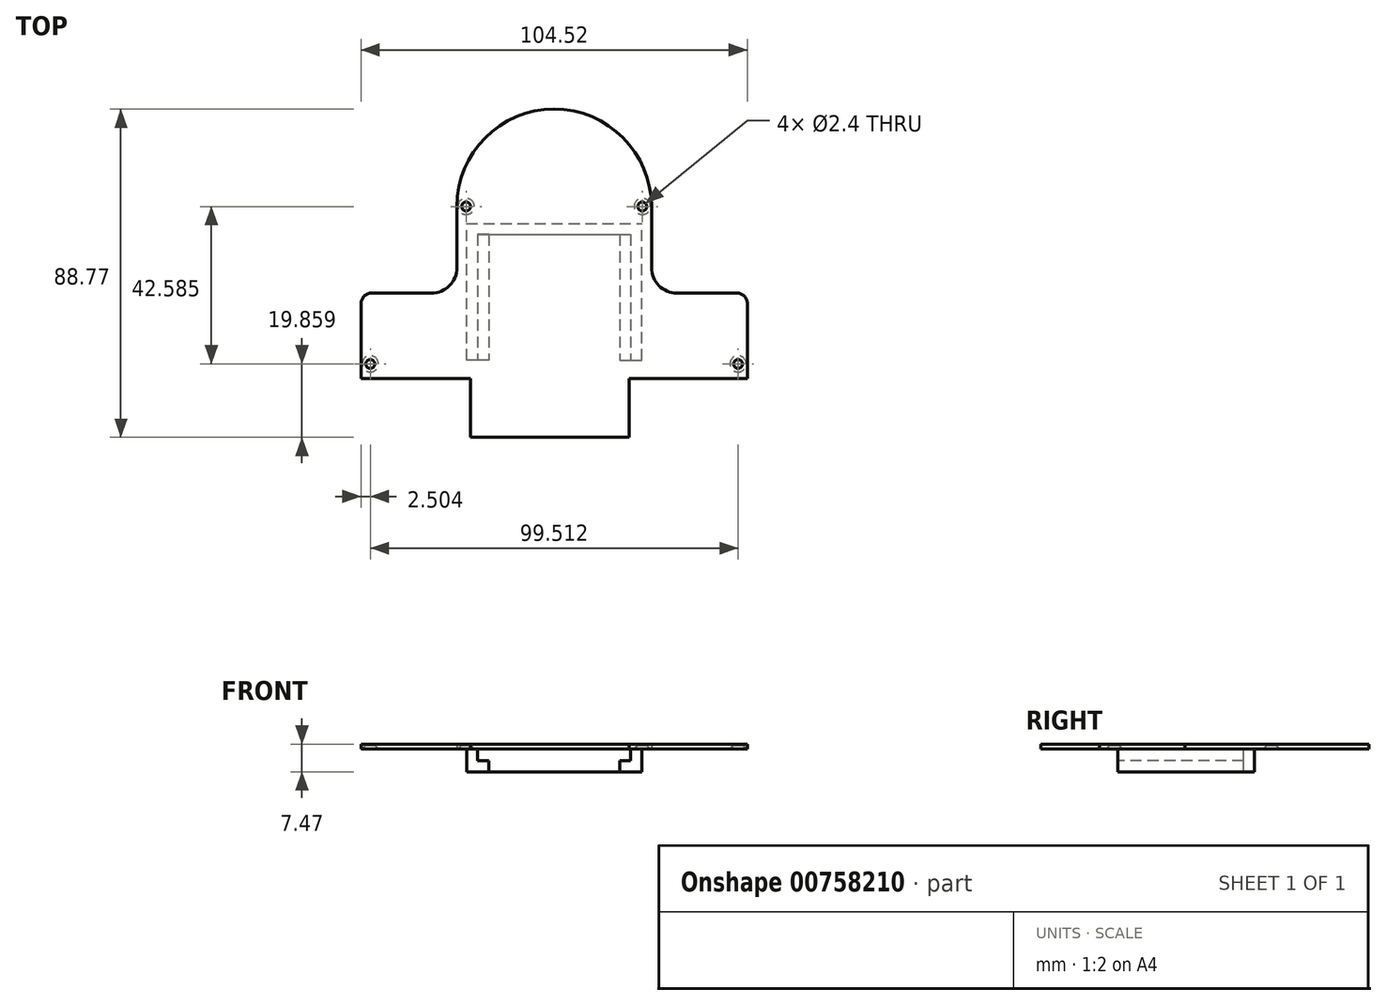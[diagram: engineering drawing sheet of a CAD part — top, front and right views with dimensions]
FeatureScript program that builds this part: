
annotation { "Feature Type Name" : "Feature", "Feature Type Description" : "" }
export const myFeature = defineFeature(function(context is Context, id is Id, definition is map)
    precondition{}
    {
        {
            var Q0;
            Q0=qCreatedBy(makeId("Top.planeOp"),FACE);
            var sketch = newSketch(context, id + "F0", { "sketchPlane" : qUnion([Q0])});
            skLineSegment(sketch, "E0.top", {"start": v(-22.63, -46.5) * mm, "end": v(20.3, -46.5) * mm});
            skLineSegment(sketch, "E0.left", {"start": v(-22.63, -30.65) * mm, "end": v(-22.63, -46.5) * mm});
            skLineSegment(sketch, "E1", {"start": v(26.33, 15.93) * mm, "end": v(26.33, -0.6) * mm});
            skLineSegment(sketch, "E2", {"start": v(33.22, -7.49) * mm, "end": v(49.42, -7.49) * mm});
            skLineSegment(sketch, "E3", {"start": v(52.26, -10.32) * mm, "end": v(52.26, -30.65) * mm});
            skLineSegment(sketch, "E4", {"start": v(-22.63, -30.65) * mm, "end": v(-52.26, -30.65) * mm});
            skLineSegment(sketch, "E5", {"start": v(-52.26, -30.65) * mm, "end": v(-52.26, -10.32) * mm});
            skLineSegment(sketch, "E6", {"start": v(-49.42, -7.49) * mm, "end": v(-33.22, -7.49) * mm});
            skLineSegment(sketch, "E7", {"start": v(-26.33, -0.6) * mm, "end": v(-26.33, 15.93) * mm});
            skArc(sketch, "E8", {"start": v(26.33, 15.93) * mm, "mid": v(0, 42.26) * mm, "end": v(-26.33, 15.93) * mm});
            skArc(sketch, "E9", {"start": v(-33.22, -7.49) * mm, "mid": v(-28.35, -5.47) * mm, "end": v(-26.33, -0.6) * mm});
            skArc(sketch, "E10", {"start": v(26.33, -0.6) * mm, "mid": v(28.35, -5.47) * mm, "end": v(33.22, -7.49) * mm});
            skArc(sketch, "E11", {"start": v(-49.42, -7.49) * mm, "mid": v(-51.43, -8.32) * mm, "end": v(-52.26, -10.32) * mm});
            skArc(sketch, "E12", {"start": v(52.26, -10.32) * mm, "mid": v(51.43, -8.32) * mm, "end": v(49.42, -7.49) * mm});
            skLineSegment(sketch, "E13", {"start": v(20.3, -46.5) * mm, "end": v(20.3, -30.65) * mm});
            skLineSegment(sketch, "E14", {"start": v(20.3, -30.65) * mm, "end": v(52.26, -30.65) * mm});
            skCircle(sketch, "E15", {"center": v(-49.76, -26.65) * mm, "radius": 2.2 * mm});
            skCircle(sketch, "E16", {"center": v(-23.83, 15.93) * mm, "radius": 2.2 * mm});
            skCircle(sketch, "E17", {"center": v(23.83, 15.93) * mm, "radius": 2.2 * mm});
            skCircle(sketch, "E18", {"center": v(49.76, -26.65) * mm, "radius": 2.2 * mm});
            skCircle(sketch, "E19", {"center": v(-49.76, -26.65) * mm, "radius": 1.2 * mm});
            skCircle(sketch, "E20", {"center": v(49.76, -26.65) * mm, "radius": 1.2 * mm});
            skCircle(sketch, "E21", {"center": v(23.83, 15.93) * mm, "radius": 1.2 * mm});
            skCircle(sketch, "E22", {"center": v(-23.83, 15.93) * mm, "radius": 1.2 * mm});
            skLineSegment(sketch, "E23", {"start": v(-20.7, 8.35) * mm, "end": v(20.7, 8.35) * mm});
            skPoint(sketch, "E24", {"position": v(0, 8.35) * mm});
            skLineSegment(sketch, "E25", {"start": v(-20.7, 8.35) * mm, "end": v(-20.7, -25.65) * mm});
            skLineSegment(sketch, "E26.bottom", {"start": v(-20.7, -25.65) * mm, "end": v(-23.7, -25.65) * mm});
            skLineSegment(sketch, "E26.top", {"start": v(-20.7, 8.35) * mm, "end": v(-23.7, 8.35) * mm});
            skLineSegment(sketch, "E26.left", {"start": v(-20.7, -25.65) * mm, "end": v(-20.7, 8.35) * mm});
            skLineSegment(sketch, "E26.right", {"start": v(-23.7, -25.65) * mm, "end": v(-23.7, 8.35) * mm});
            skLineSegment(sketch, "E27.bottom", {"start": v(20.7, 8.35) * mm, "end": v(23.7, 8.35) * mm});
            skLineSegment(sketch, "E27.top", {"start": v(20.7, -25.65) * mm, "end": v(23.7, -25.65) * mm});
            skLineSegment(sketch, "E27.left", {"start": v(20.7, 8.35) * mm, "end": v(20.7, -25.65) * mm});
            skLineSegment(sketch, "E27.right", {"start": v(23.7, 8.35) * mm, "end": v(23.7, -25.65) * mm});
            skLineSegment(sketch, "E28.bottom", {"start": v(-23.7, 8.35) * mm, "end": v(23.7, 8.35) * mm});
            skLineSegment(sketch, "E28.top", {"start": v(-23.7, 11.35) * mm, "end": v(23.7, 11.35) * mm});
            skLineSegment(sketch, "E28.left", {"start": v(-23.7, 8.35) * mm, "end": v(-23.7, 11.35) * mm});
            skLineSegment(sketch, "E28.right", {"start": v(23.7, 8.35) * mm, "end": v(23.7, 11.35) * mm});
            skSolve(sketch);
        }
        {
            var Q0;
            Q0=makeQuery(id+"F0.imprint","IMPRINT",FACE,{"disambiguationData":[TD([[makeQuery(id+"F0.imprint","IMPRINT",EDGE,{"derivedFrom":sQuery(id+"F0.wireOp",EDGE,"E0.top")}),1.0]])]});
            var Q1;
            Q1=makeQuery(id+"F0.imprint","IMPRINT",FACE,{"disambiguationData":[TD([[makeQuery(id+"F0.imprint","IMPRINT",EDGE,{"derivedFrom":sQuery(id+"F0.wireOp",EDGE,"E16")}),1.0]])]});
            var Q2;
            Q2=makeQuery(id+"F0.imprint","IMPRINT",FACE,{"disambiguationData":[TD([[makeQuery(id+"F0.imprint","IMPRINT",EDGE,{"derivedFrom":sQuery(id+"F0.wireOp",EDGE,"E17")}),1.0]])]});
            var Q3;
            Q3=makeQuery(id+"F0.imprint","IMPRINT",FACE,{"disambiguationData":[TD([[makeQuery(id+"F0.imprint","IMPRINT",EDGE,{"derivedFrom":sQuery(id+"F0.wireOp",EDGE,"E18")}),1.0]])]});
            var Q4;
            Q4=makeQuery(id+"F0.imprint","IMPRINT",FACE,{"disambiguationData":[TD([[makeQuery(id+"F0.imprint","IMPRINT",EDGE,{"derivedFrom":sQuery(id+"F0.wireOp",EDGE,"E19")}),1.0]])]});
            var Q5;
            Q5=makeQuery(id+"F0.imprint","IMPRINT",FACE,{"disambiguationData":[TD([[makeQuery(id+"F0.imprint","IMPRINT",EDGE,{"derivedFrom":sQuery(id+"F0.wireOp",EDGE,"E15")}),1.0]])]});
            var Q6;
            Q6=makeQuery(id+"F0.imprint","IMPRINT",FACE,{"disambiguationData":[TD([[makeQuery(id+"F0.imprint","IMPRINT",EDGE,{"derivedFrom":sQuery(id+"F0.wireOp",EDGE,"E22")}),1.0]])]});
            var Q7;
            Q7=makeQuery(id+"F0.imprint","IMPRINT",FACE,{"disambiguationData":[TD([[makeQuery(id+"F0.imprint","IMPRINT",EDGE,{"derivedFrom":sQuery(id+"F0.wireOp",EDGE,"E21")}),1.0]])]});
            var Q8;
            Q8=makeQuery(id+"F0.imprint","IMPRINT",FACE,{"disambiguationData":[TD([[makeQuery(id+"F0.imprint","IMPRINT",EDGE,{"derivedFrom":sQuery(id+"F0.wireOp",EDGE,"E20")}),1.0]])]});
            var Q9;
            Q9=makeQuery(id+"F0.imprint","IMPRINT",FACE,{"disambiguationData":[TD([[makeQuery(id+"F0.imprint","IMPRINT",EDGE,{"derivedFrom":sQuery(id+"F0.wireOp",EDGE,"E25")}),-1.0]])]});
            var Q10;
            Q10=makeQuery(id+"F0.imprint","IMPRINT",FACE,{"disambiguationData":[TD([[makeQuery(id+"F0.imprint","IMPRINT",EDGE,{"derivedFrom":sQuery(id+"F0.wireOp",EDGE,"E23")}),1.0]])]});
            var Q11;
            Q11=makeQuery(id+"F0.imprint","IMPRINT",FACE,{"disambiguationData":[TD([[makeQuery(id+"F0.imprint","IMPRINT",EDGE,{"derivedFrom":sQuery(id+"F0.wireOp",EDGE,"E27.bottom")}),-1.0]])]});
            extrude(context, id + "F1", {"entities" : qUnion([Q0, Q1, Q2, Q3, Q4, Q5, Q6, Q7, Q8, Q9, Q10, Q11]), "depth" : 1.27 * mm, "offsetDistance" : 25 * mm});
        }
        {
            var Q0;
            Q0=sQuery(id+"F0.wireOp",VERTEX,"E15.center");
            var Q1;
            Q1=sQuery(id+"F0.wireOp",VERTEX,"E18.center");
            var Q2;
            Q2=sQuery(id+"F0.wireOp",VERTEX,"E16.center");
            var Q3;
            Q3=sQuery(id+"F0.wireOp",VERTEX,"E17.center");
            var Q4;
            Q4=makeQuery(id+"F1.opExtrude","SWEPT_BODY",BODY,{"disambiguationData":[OSD([sQuery(id+"F0.wireOp",EDGE,"E0.top"),sQuery(id+"F0.wireOp",EDGE,"E0.left"),sQuery(id+"F0.wireOp",EDGE,"E1"),sQuery(id+"F0.wireOp",EDGE,"E2"),sQuery(id+"F0.wireOp",EDGE,"E3"),sQuery(id+"F0.wireOp",EDGE,"E4"),sQuery(id+"F0.wireOp",EDGE,"E5"),sQuery(id+"F0.wireOp",EDGE,"E6"),sQuery(id+"F0.wireOp",EDGE,"E7"),sQuery(id+"F0.wireOp",EDGE,"E8"),sQuery(id+"F0.wireOp",EDGE,"E9"),sQuery(id+"F0.wireOp",EDGE,"E10"),sQuery(id+"F0.wireOp",EDGE,"E11"),sQuery(id+"F0.wireOp",EDGE,"E12"),sQuery(id+"F0.wireOp",EDGE,"E13"),sQuery(id+"F0.wireOp",EDGE,"E14")])]});
            hole(context, id + "F2", {"style" : HoleStyle.C_SINK, "endStyle" : HoleEndStyle.THROUGH, "oppositeDirection" : true, "holeDiameter" : 2.4 * mm, "cSinkDiameter" : 4.4 * mm, "cSinkAngle" : 90 * degree, "majorDiameter" : 5 * mm, "isTappedThrough" : true, "tappedDepth" : 12 * mm, "tapClearance" : 3, "locations" : qUnion([Q0, Q1, Q2, Q3]), "scope" : qUnion([Q4])});
        }
        {
            var Q0;
            Q0=makeQuery(id+"F0.imprint","IMPRINT",FACE,{"disambiguationData":[TD([[makeQuery(id+"F0.imprint","IMPRINT",EDGE,{"derivedFrom":sQuery(id+"F0.wireOp",EDGE,"E25")}),-1.0]])]});
            var Q1;
            Q1=makeQuery(id+"F0.imprint","IMPRINT",FACE,{"disambiguationData":[TD([[makeQuery(id+"F0.imprint","IMPRINT",EDGE,{"derivedFrom":sQuery(id+"F0.wireOp",EDGE,"E23")}),1.0]])]});
            var Q2;
            Q2=makeQuery(id+"F0.imprint","IMPRINT",FACE,{"disambiguationData":[TD([[makeQuery(id+"F0.imprint","IMPRINT",EDGE,{"derivedFrom":sQuery(id+"F0.wireOp",EDGE,"E27.bottom")}),-1.0]])]});
            extrude(context, id + "F3", {"entities" : qUnion([Q0, Q1, Q2]), "operationType" : NewBodyOperationType.ADD, "oppositeDirection" : true, "depth" : 6.2 * mm, "offsetDistance" : 25 * mm});
        }
        {
            var Q0;
            Q0=makeQuery(id+"F3.opExtrude","SWEPT_FACE",FACE,{"disambiguationData":[OSD([sQuery(id+"F0.wireOp",EDGE,"E25")])]});
            var sketch = newSketch(context, id + "F4", { "sketchPlane" : qUnion([Q0])});
            skLineSegment(sketch, "E29", {"start": v(8.35, -3.2) * mm, "end": v(-25.65, -3.2) * mm});
            skPoint(sketch, "E29.endSnap0", {"position": v(-25.65, -3.1) * mm});
            skSolve(sketch);
        }
        {
            var Q0;
            Q0=makeQuery(id+"F3.opExtrude","SWEPT_FACE",FACE,{"disambiguationData":[OSD([sQuery(id+"F0.wireOp",EDGE,"E27.left")])]});
            var sketch = newSketch(context, id + "F5", { "sketchPlane" : qUnion([Q0])});
            skLineSegment(sketch, "E30", {"start": v(-8.35, -3.2) * mm, "end": v(25.65, -3.2) * mm});
            skSolve(sketch);
        }
        {
            var Q0;
            {var subQ0=sQuery(id+"F5.wireOp",EDGE,"E30");Q0=makeQuery(id+"F5.imprint","IMPRINT",FACE,{"disambiguationData":[TD([[makeQuery(id+"F5.imprint","IMPRINT",EDGE,{"derivedFrom":subQ0}),-1.0]])]});}
            extrude(context, id + "F6", {"entities" : qUnion([Q0]), "operationType" : NewBodyOperationType.ADD, "depth" : 3 * mm, "offsetDistance" : 25 * mm});
        }
        {
            var Q0;
            {var subQ0=sQuery(id+"F4.wireOp",EDGE,"E29");Q0=makeQuery(id+"F4.imprint","IMPRINT",FACE,{"disambiguationData":[TD([[makeQuery(id+"F4.imprint","IMPRINT",EDGE,{"derivedFrom":subQ0}),1.0]])]});}
            extrude(context, id + "F7", {"entities" : qUnion([Q0]), "operationType" : NewBodyOperationType.ADD, "depth" : 3 * mm, "offsetDistance" : 25 * mm});
        }
    });
